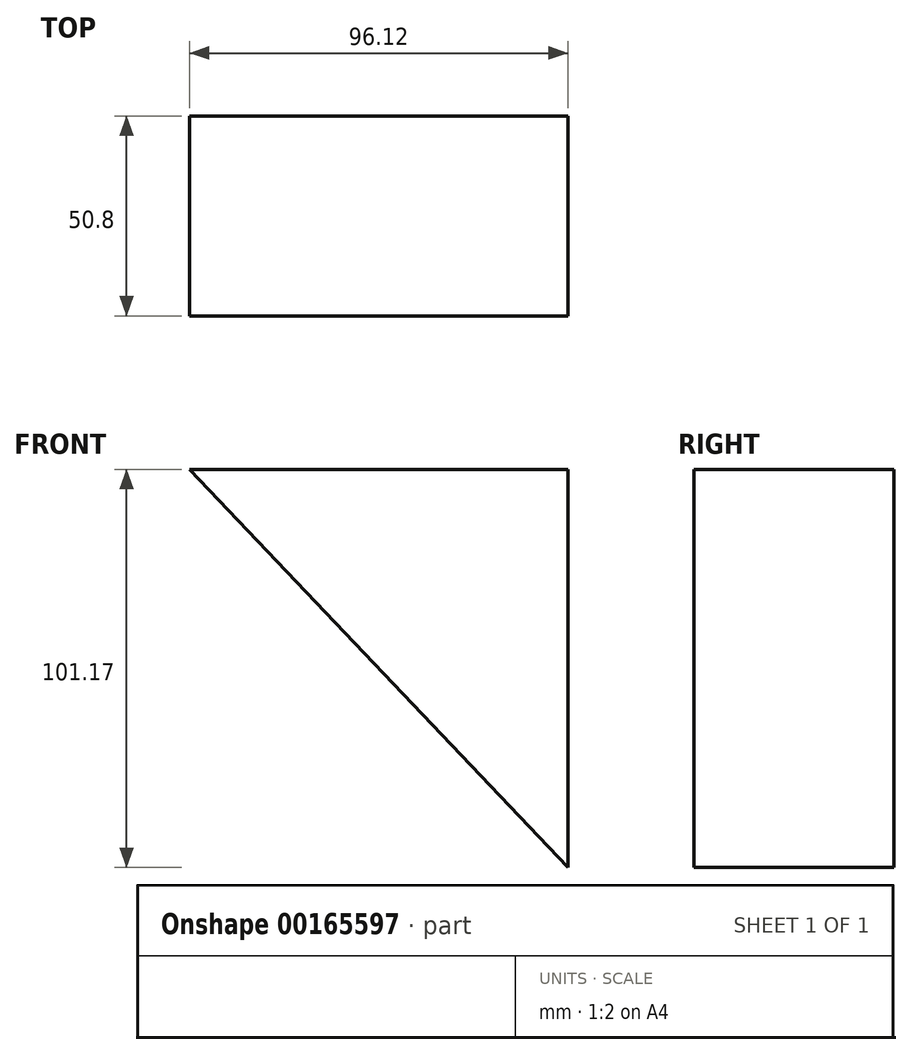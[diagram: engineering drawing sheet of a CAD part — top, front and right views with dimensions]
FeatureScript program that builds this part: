
annotation { "Feature Type Name" : "Feature", "Feature Type Description" : "" }
export const myFeature = defineFeature(function(context is Context, id is Id, definition is map)
    precondition{}
    {
        {
            var Q0;
            Q0=qCreatedBy(makeId("Front.planeOp"),FACE);
            var sketch = newSketch(context, id + "F0", { "sketchPlane" : qUnion([Q0])});
            skLineSegment(sketch, "E0", {"start": v(-47.64, 52.55) * mm, "end": v(48.48, 52.55) * mm});
            skLineSegment(sketch, "E1", {"start": v(48.48, 52.55) * mm, "end": v(48.48, -48.62) * mm});
            skLineSegment(sketch, "E2", {"start": v(48.48, -48.62) * mm, "end": v(-47.64, 52.55) * mm});
            skSolve(sketch);
        }
        {
            var Q0;
            Q0 = qSketchRegion(id + "F0", true);
            extrude(context, id + "F1", {"entities" : qUnion([Q0]), "depth" : 50.8 * mm});
        }
    });
